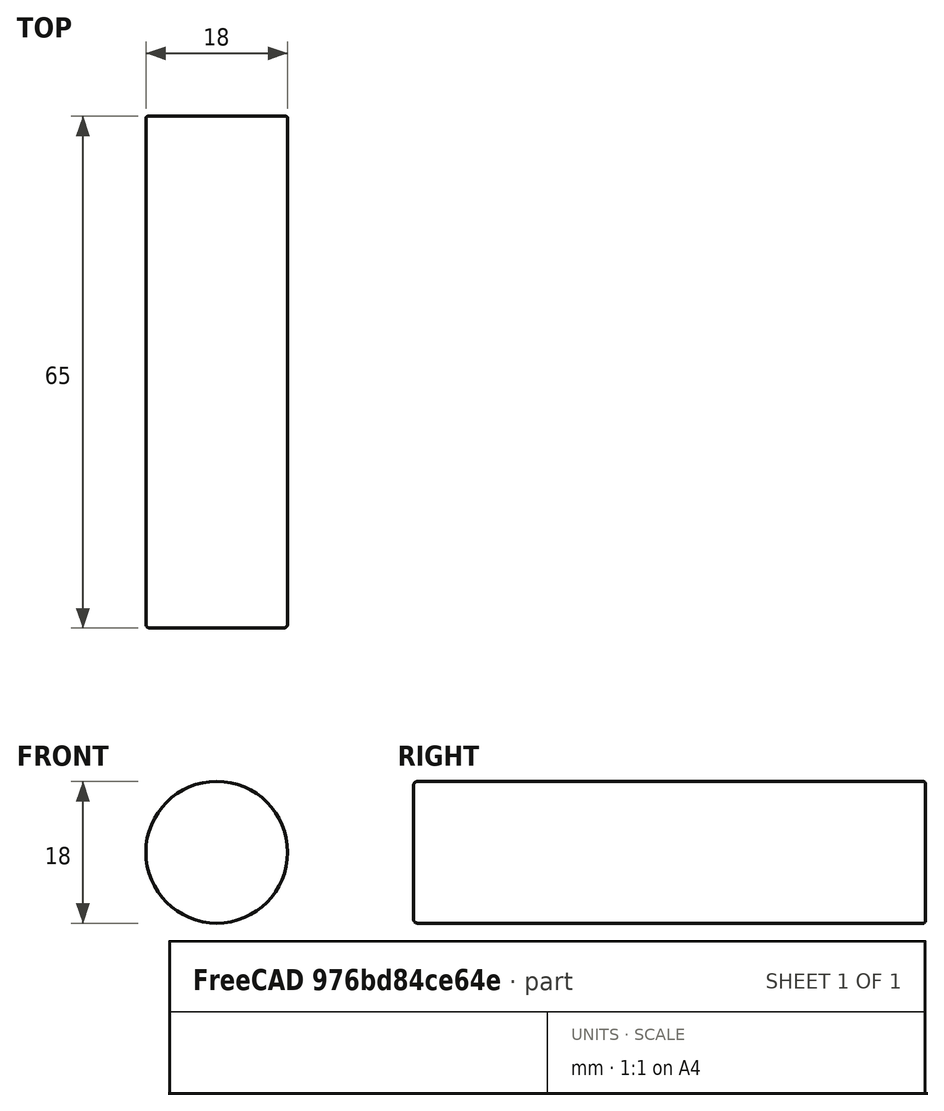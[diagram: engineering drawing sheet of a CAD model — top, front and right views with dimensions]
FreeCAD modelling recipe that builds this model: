
FCSTD DOCUMENT  (FreeCAD 2021.519R24301 +3652 (Git))
Label: ASR00050-1_18650_2500mAh
License: Other
objects: TechDraw::DrawViewAnnotation×5, Sketcher::SketchObject×4, PartDesign::Pad×4, TechDraw::DrawViewDimension×4, TechDraw::DrawViewPart×3, PartDesign::Fillet×2, Mesh::Feature×1, TechDraw::DrawSVGTemplate×1, PartDesign::Plane×1, PartDesign::Body×1, TechDraw::DrawPage×1
note: 24 computed .brp shape members not serialized (recipe doc carries the construction recipe); baked Part::Feature solids carry a one-line shape summary decoded from their .brp

FEATURE [Sketcher::SketchObject] Sketch
  FullyConstrained = true
  MapMode = 5
  Placement = pos=(0,0,0) rot=(1,0,0;1.5708rad)
  Support = -> [XZ_Plane]
  sketch-geometry (1):
    g0: Circle CenterX=0 CenterY=0 CenterZ=0 NormalX=0 NormalY=0 NormalZ=1 AngleXU=0 Radius=9
  constraints (2):
    c: Coincident(g0,g-1)
    c: Diameter(g0) = 18
FEATURE [PartDesign::Pad] Pad
  ClaimChildren = false
  Direction = (1,1,1)
  Fit = 0
  FitJoin = 0
  InnerFit = 0
  InnerFitJoin = 0
  InnerTaperAngle = 0
  InnerTaperAngleRev = 0
  Length = 65
  Length2 = 100
  Midplane = true
  NewSolid = false
  Placement = pos=(0,0,0) rot=(1,0,0;1.5708rad)
  Profile = -> Sketch
  Suppress = false
  Type = 0
FEATURE [PartDesign::Fillet] Fillet
  Base = -> Pad [Edge3]
  BaseFeature = -> Pad
  NewSolid = false
  Placement = pos=(0,0,0) rot=(1,0,0;1.5708rad)
  Radius = 0.5
  SupportTransform = false
  Suppress = false
FEATURE [PartDesign::Fillet] Fillet001
  Base = -> Fillet [Edge3]
  BaseFeature = -> Fillet
  NewSolid = false
  Placement = pos=(0,0,0) rot=(1,0,0;1.5708rad)
  Radius = 0.25
  SupportTransform = false
  Suppress = false
FEATURE [Sketcher::SketchObject] Sketch001
  FullyConstrained = true
  MapMode = 5
  Placement = pos=(0,-32.5,2.16e-14) rot=(1,0,0;1.5708rad)
  Support = -> [Fillet001]
  sketch-geometry (1):
    g0: Circle CenterX=0 CenterY=0 CenterZ=0 NormalX=0 NormalY=0 NormalZ=1 AngleXU=0 Radius=5
  constraints (2):
    c: Coincident(g0,g-1)
    c: Diameter(g0) = 10
FEATURE [PartDesign::Pad] Pad001
  BaseFeature = -> Fillet001
  ClaimChildren = false
  Direction = (1,1,1)
  Fit = 0
  FitJoin = 0
  InnerFit = 0
  InnerFitJoin = 0
  InnerTaperAngle = 0
  InnerTaperAngleRev = 0
  Length = 10
  Length2 = 100
  NewSolid = false
  Placement = pos=(0,0,0) rot=(1,0,0;1.5708rad)
  Profile = -> Sketch001
  Reversed = true
  Suppress = false
  Type = 0
FEATURE [Sketcher::SketchObject] Sketch002
  ExternalGeometry = -> [Pad001]
  FullyConstrained = true
  MapMode = 5
  Placement = pos=(0,-32.5,3.61e-14) rot=(1,0,0;1.5708rad)
  Support = -> [Pad001]
  sketch-geometry (3):
    g0: Circle CenterX=0 CenterY=0 CenterZ=0 NormalX=0 NormalY=0 NormalZ=1 AngleXU=0 Radius=6
    g1: LineSegment [constr] StartX=5 StartY=0 StartZ=0 EndX=6 EndY=0 EndZ=0
    g2: Circle CenterX=0 CenterY=0 CenterZ=0 NormalX=0 NormalY=0 NormalZ=1 AngleXU=0 Radius=5
  constraints (8):
    c: Coincident(g0,g-1)
    c: PointOnObject(g1,g-3)
    c: PointOnObject(g1,g0)
    c: Horizontal(g1)
    c: PointOnObject(g1,g-1)
    c: DistanceX(g1,g1) = 1
    c: Coincident(g2,g0)
    c: PointOnObject(g1,g2)
FEATURE [PartDesign::Pad] Pad002
  BaseFeature = -> Pad001
  ClaimChildren = false
  Direction = (1,1,1)
  Fit = 0
  FitJoin = 0
  InnerFit = 0
  InnerFitJoin = 0
  InnerTaperAngle = 0
  InnerTaperAngleRev = 0
  Length = 10
  Length2 = 100
  NewSolid = false
  Placement = pos=(0,0,0) rot=(1,0,0;1.5708rad)
  Profile = -> Sketch002
  Reversed = true
  Suppress = false
  Type = 0
FEATURE [Sketcher::SketchObject] Sketch003
  FullyConstrained = true
  MapMode = 5
  Placement = pos=(0,32.5,-5.05e-14) rot=(-1,0,0;1.5708rad)
  Support = -> [Pad002]
  sketch-geometry (1):
    g0: Circle CenterX=0 CenterY=0 CenterZ=0 NormalX=0 NormalY=0 NormalZ=1 AngleXU=0 Radius=7
  constraints (2):
    c: Coincident(g0,g-1)
    c: Diameter(g0) = 14
FEATURE [PartDesign::Pad] Pad003
  BaseFeature = -> Pad002
  ClaimChildren = false
  ColoredElements = -> Pad003 [Face1,Face2,Face3,Face4,Face5,Face7]
  Direction = (1,1,1)
  Fit = 0
  FitJoin = 0
  InnerFit = 0
  InnerFitJoin = 0
  InnerTaperAngle = 0
  InnerTaperAngleRev = 0
  Length = 10
  Length2 = 100
  NewSolid = false
  Placement = pos=(0,0,0) rot=(1,0,0;1.5708rad)
  Profile = -> Sketch003
  Reversed = true
  Suppress = false
  Type = 0
FEATURE [Mesh::Feature] Mesh  label="Body (Meshed)"
FEATURE [TechDraw::DrawSVGTemplate] Template
  Height = 210
  Orientation = 1
  Width = 297
FEATURE [PartDesign::Plane] DatumPlane
  AttachmentOffset = pos=(-9,0,0) rot=(0,-1,0;1.5708rad)
  Length = 65
  MapMode = 5
  MinimumLength = 10
  MinimumWidth = 10
  Placement = pos=(-9,-32.5,4.33e-14) rot=(0.57735,-0.57735,-0.57735;2.0944rad)
  ResizeMode = 0
  Support = -> [Pad003]
  Width = 17.9843
FEATURE [PartDesign::Body] Body
  AutoGroupSolids = false
  ExportMode = 0
  Group = -> [Sketch,Pad,Fillet,Fillet001,Sketch001,Pad001,Sketch002,Pad002,Sketch003,Pad003,DatumPlane]
  Origin = -> Origin
  Tip = -> Pad003
  _ExportChildren = -> [Pad,Fillet,Fillet001,Pad001,Pad002,Pad003,DatumPlane]
  _GroupVersion = 1
FEATURE [TechDraw::DrawViewPart] View
  CoarseView = false
  Direction = (0,-1,0)
  Focus = 100
  HardHidden = false
  IsoCount = 0
  IsoHidden = false
  IsoVisible = false
  LockPosition = false
  Perspective = false
  Rotation = 0
  Scale = 2
  ScaleType = 0
  SeamHidden = false
  SeamVisible = true
  SmoothHidden = false
  SmoothVisible = true
  Source = -> [Body]
  X = 105
  XDirection = (1,0,0)
  Y = 150
FEATURE [TechDraw::DrawViewPart] View002
  CoarseView = false
  Direction = (0,1,0)
  Focus = 100
  HardHidden = false
  IsoCount = 0
  IsoHidden = false
  IsoVisible = false
  LockPosition = false
  Perspective = false
  Rotation = 0
  Scale = 2
  ScaleType = 0
  SeamHidden = false
  SeamVisible = true
  SmoothHidden = false
  SmoothVisible = true
  Source = -> [Body]
  X = 185
  XDirection = (-1,0,0)
  Y = 150
FEATURE [TechDraw::DrawViewAnnotation] Annotation
  Font = MS Shell Dlg 2
  LineSpace = 80
  LockPosition = false
  MaxWidth = -1
  Rotation = 0
  ScaleType = 0
  Text = + TERMINAL VIEW
  TextSize = 5.25
  TextStyle = 0
  X = 105
  Y = 178
FEATURE [TechDraw::DrawViewAnnotation] Annotation001
  Font = MS Shell Dlg 2
  LineSpace = 80
  LockPosition = false
  MaxWidth = -1
  Rotation = 0
  ScaleType = 0
  Text = - TERMINAL VIEW
  TextSize = 5.25
  TextStyle = 0
  X = 185
  Y = 178
FEATURE [TechDraw::DrawViewDimension] Dimension001
  Arbitrary = false
  ArbitraryTolerances = false
  EqualTolerance = true
  FormatSpec = ⌀%.1f
  FormatSpecOverTolerance = %+.1f
  FormatSpecUnderTolerance = %+.1f
  Inverted = false
  LockPosition = false
  MeasureType = 1
  OverTolerance = 0.25
  References2D = -> [View]
  Rotation = 0
  ScaleType = 0
  TheoreticalExact = false
  Type = 5
  UnderTolerance = -0.25
  X = 28.6709
  Y = -14.3355
FEATURE [TechDraw::DrawViewDimension] Dimension002
  Arbitrary = false
  ArbitraryTolerances = false
  EqualTolerance = true
  FormatSpec = ⌀%.1f
  FormatSpecOverTolerance = %+.1f
  FormatSpecUnderTolerance = %+.1f
  Inverted = false
  LockPosition = false
  MeasureType = 1
  OverTolerance = 0.25
  References2D = -> [View002]
  Rotation = 0
  ScaleType = 0
  TheoreticalExact = false
  Type = 5
  UnderTolerance = -0.25
  X = 29.4417
  Y = -15.1062
FEATURE [TechDraw::DrawViewAnnotation] Annotation004
  Font = MS Shell Dlg 2
  LineSpace = 80
  LockPosition = false
  MaxWidth = -1
  Rotation = 0
  ScaleType = 0
  Text = SIDE VIEW
  TextSize = 5.25
  TextStyle = 0
  X = 145
  Y = 55.2664
FEATURE [TechDraw::DrawViewPart] View003
  CoarseView = false
  Direction = (0,0,1)
  Focus = 100
  HardHidden = false
  IsoCount = 0
  IsoHidden = false
  IsoVisible = false
  LockPosition = false
  Perspective = false
  Rotation = 0
  Scale = 2
  ScaleType = 0
  SeamHidden = false
  SeamVisible = true
  SmoothHidden = false
  SmoothVisible = true
  Source = -> [Body]
  X = 145
  XDirection = (0,1,0)
  Y = 90
FEATURE [TechDraw::DrawViewAnnotation] Annotation005
  Font = MS Shell Dlg 2
  LineSpace = 80
  LockPosition = false
  MaxWidth = -1
  Rotation = 0
  ScaleType = 0
  Text = -
  TextSize = 5.25
  TextStyle = 0
  X = 200
  Y = 90
FEATURE [TechDraw::DrawViewAnnotation] Annotation006
  Font = MS Shell Dlg 2
  LineSpace = 80
  LockPosition = false
  MaxWidth = -1
  Rotation = 0
  ScaleType = 0
  Text = +
  TextSize = 5.25
  TextStyle = 0
  X = 90
  Y = 90
FEATURE [TechDraw::DrawViewDimension] Dimension
  Arbitrary = false
  ArbitraryTolerances = false
  EqualTolerance = true
  FormatSpec = %.1f
  FormatSpecOverTolerance = %+.1f
  FormatSpecUnderTolerance = %+.1f
  Inverted = false
  LockPosition = false
  MeasureType = 1
  OverTolerance = 0.5
  References2D = -> [View003]
  Rotation = 0
  ScaleType = 0
  TheoreticalExact = false
  Type = 2
  UnderTolerance = -0.5
  X = -78.7203
  Y = 0.841079
FEATURE [TechDraw::DrawViewDimension] Dimension003
  Arbitrary = false
  ArbitraryTolerances = false
  EqualTolerance = true
  FormatSpec = %.1f
  FormatSpecOverTolerance = %+.1f
  FormatSpecUnderTolerance = %+.1f
  Inverted = false
  LockPosition = false
  MeasureType = 1
  OverTolerance = 0.5
  References2D = -> [View003]
  Rotation = 0
  ScaleType = 0
  TheoreticalExact = false
  Type = 1
  UnderTolerance = -0.5
  X = -5.20643
  Y = 27.325
FEATURE [TechDraw::DrawPage] Page
  KeepUpdated = true
  NextBalloonIndex = 1
  ProjectionType = 0
  Template = -> Template
  Views = -> [View,View002,Annotation,Annotation001,Dimension001,Dimension002,Annotation004,View003,Annotation005,Annotation006,Dimension,Dimension003]
